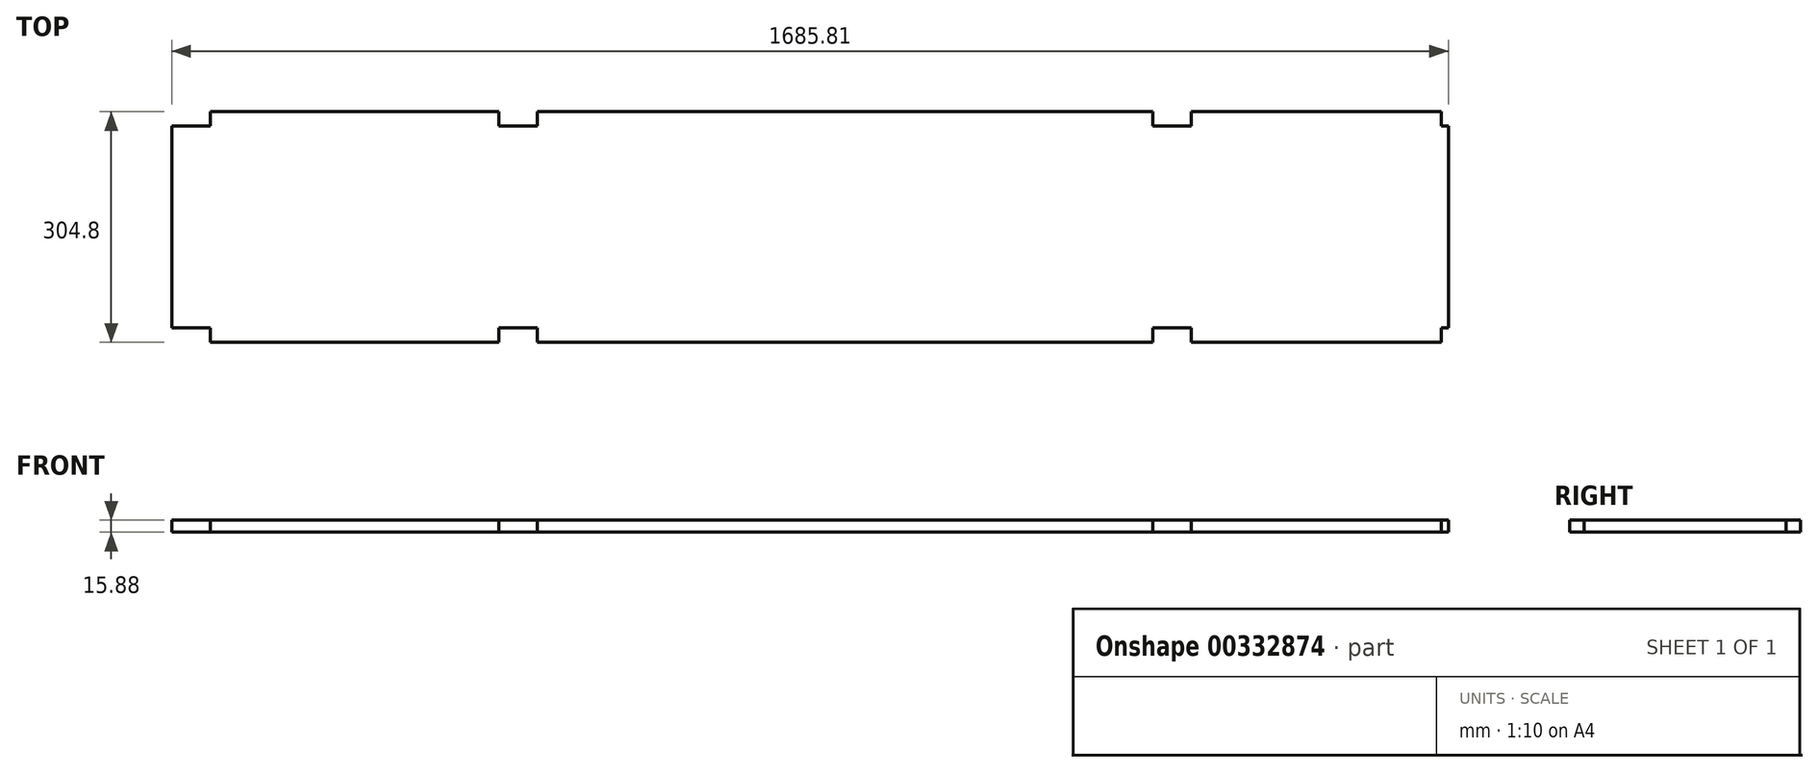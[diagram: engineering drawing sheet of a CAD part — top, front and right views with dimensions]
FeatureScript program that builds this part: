
annotation { "Feature Type Name" : "Feature", "Feature Type Description" : "" }
export const myFeature = defineFeature(function(context is Context, id is Id, definition is map)
    precondition{}
    {
        {
            var Q0;
            Q0=qCreatedBy(makeId("Top.planeOp"),FACE);
            var sketch = newSketch(context, id + "F0", { "sketchPlane" : qUnion([Q0])});
            skLineSegment(sketch, "E0.top", {"start": v(-444.5, 425.45) * mm, "end": v(-114.41, 425.45) * mm});
            skPoint(sketch, "E0.middle", {"position": v(0, 0) * mm});
            skPoint(sketch, "E1.orphan", {"position": v(-495.3, -425.45) * mm});
            skLineSegment(sketch, "E2", {"start": v(-444.5, 120.65) * mm, "end": v(-114.41, 120.65) * mm});
            skLineSegment(sketch, "E3.top", {"start": v(-495.3, 139.7) * mm, "end": v(-444.5, 139.7) * mm});
            skLineSegment(sketch, "E3.right", {"start": v(-444.5, 120.65) * mm, "end": v(-444.5, 139.7) * mm});
            skLineSegment(sketch, "E4.top", {"start": v(-495.3, 406.4) * mm, "end": v(-444.5, 406.4) * mm});
            skLineSegment(sketch, "E4.right", {"start": v(-444.5, 425.45) * mm, "end": v(-444.5, 406.4) * mm});
            skPoint(sketch, "E5.orphan", {"position": v(-495.3, 425.45) * mm});
            skPoint(sketch, "E6.orphan", {"position": v(495.3, -425.45) * mm});
            skPoint(sketch, "E7.orphan", {"position": v(495.3, 425.45) * mm});
            skLineSegment(sketch, "E8.top", {"start": v(-114.41, 139.7) * mm, "end": v(-104.89, 139.7) * mm});
            skLineSegment(sketch, "E8.left", {"start": v(-114.41, 120.65) * mm, "end": v(-114.41, 139.7) * mm});
            skPoint(sketch, "E9.orphan", {"position": v(190.5, -158.86) * mm});
            skPoint(sketch, "E10.orphan", {"position": v(-89.01, 120.65) * mm});
            skLineSegment(sketch, "E11.bottom", {"start": v(-114.41, 406.4) * mm, "end": v(-104.89, 406.4) * mm});
            skLineSegment(sketch, "E11.left", {"start": v(-114.41, 406.4) * mm, "end": v(-114.41, 425.45) * mm});
            skLineSegment(sketch, "E12.bottom", {"start": v(-495.3, 120.65) * mm, "end": v(-1308.1, 120.65) * mm});
            skLineSegment(sketch, "E12.top", {"start": v(-495.3, 425.45) * mm, "end": v(-1308.1, 425.45) * mm});
            skLineSegment(sketch, "E12.left", {"start": v(-495.3, 120.65) * mm, "end": v(-495.3, 139.7) * mm});
            skLineSegment(sketch, "E12.right", {"start": v(-1790.7, 139.7) * mm, "end": v(-1790.7, 406.4) * mm});
            skLineSegment(sketch, "E13.trimOffspring", {"start": v(-495.3, 406.4) * mm, "end": v(-495.3, 425.45) * mm});
            skLineSegment(sketch, "E14.top", {"start": v(-1790.7, 406.4) * mm, "end": v(-1739.9, 406.4) * mm});
            skLineSegment(sketch, "E14.right", {"start": v(-1739.9, 425.45) * mm, "end": v(-1739.9, 406.4) * mm});
            skLineSegment(sketch, "E15.bottom", {"start": v(-1790.7, 139.7) * mm, "end": v(-1739.9, 139.7) * mm});
            skLineSegment(sketch, "E15.right", {"start": v(-1739.9, 139.7) * mm, "end": v(-1739.9, 120.65) * mm});
            skLineSegment(sketch, "E16.bottom", {"start": v(-1308.1, 406.4) * mm, "end": v(-1358.9, 406.4) * mm});
            skLineSegment(sketch, "E16.left", {"start": v(-1308.1, 406.4) * mm, "end": v(-1308.1, 425.45) * mm});
            skLineSegment(sketch, "E16.right", {"start": v(-1358.9, 406.4) * mm, "end": v(-1358.9, 425.45) * mm});
            skLineSegment(sketch, "E17.bottom", {"start": v(-1358.9, 139.7) * mm, "end": v(-1308.1, 139.7) * mm});
            skLineSegment(sketch, "E17.left", {"start": v(-1358.9, 139.7) * mm, "end": v(-1358.9, 120.65) * mm});
            skLineSegment(sketch, "E17.right", {"start": v(-1308.1, 139.7) * mm, "end": v(-1308.1, 120.65) * mm});
            skPoint(sketch, "E18.orphan", {"position": v(-1790.7, 425.45) * mm});
            skLineSegment(sketch, "E19.trimOffspring", {"start": v(-1358.9, 120.65) * mm, "end": v(-1739.9, 120.65) * mm});
            skLineSegment(sketch, "E20.trimOffspring", {"start": v(-1358.9, 425.45) * mm, "end": v(-1739.9, 425.45) * mm});
            skPoint(sketch, "E21.orphan", {"position": v(-1358.9, 437.81) * mm});
            skPoint(sketch, "E22.top.start.orphan", {"position": v(476.25, -374.76) * mm});
            skPoint(sketch, "E23.orphan", {"position": v(476.25, -184.26) * mm});
            skPoint(sketch, "E24.orphan", {"position": v(209.55, -184.26) * mm});
            skLineSegment(sketch, "E25", {"start": v(-104.89, 406.4) * mm, "end": v(-104.89, 139.7) * mm});
            skPoint(sketch, "E26.end.orphan", {"position": v(-71.05, 102.69) * mm});
            skPoint(sketch, "E27.start.orphan", {"position": v(172.54, -140.9) * mm});
            skSolve(sketch);
        }
        {
            var Q0;
            Q0=qSketchRegion(id+"F0",true);
            extrude(context, id + "F1", {"entities" : qUnion([Q0]), "depth" : 15.88 * mm});
        }
    });
